# Revit family: HUNTER_I-40-06-SS
name_source: partatom
category: Sprinklers
revit_build: Autodesk Revit 2017 (Build: 20160225_1515(x64)
units: mm (PartAtom-declared; Revit-internal decimal feet)

## family parameters
Always vertical = Yes
Cut with Voids When Loaded = No
Maintain Annotation Orientation = No
OmniClass Number = 23.11.27.15.11.11
OmniClass Title = Installed Sprinkler Heads
Part Type = Normal
Room Calculation Point = No
Round Connector Dimension = Use Diameter
Shared = Yes
Work Plane-Based = No

## types (12) — shared parameters
Arc Max = 360.00°
Arc Min = 50.00°
Assembly Code = G2050700
Body Height = 200 mm  [stored 0.656168 ft]
Body Material = Hunter® ABS Plastic
Connection_Dia = 30 mm  [stored 0.0984252 ft]
Diameter = 610 mm
Exposed Diameter = 50 mm  [stored 0.164042 ft]
Inlet Size = 1" BSP
Keynote = 328423.02
Manufacturer = Hunter® Industries
Pop Up Height = 100 mm  [stored 0.328084 ft]
Pop Up Material = Hunter® Stainless Steel
Show 2D Symbol = Yes
Show Water Spray = Yes
Trajectory Angle = 25.00°
Type Comments = Rotor I-40-04 with Plastic Riser
Type Image = <None>
URL = https://www.hunterindustries.com
Water = Water
Water Pattern = Water Arc

## per-type parameters (varying)
| type | Description | Model | Nozzle Size | Nozzle Tag | Precipitation Rate | Pressure | Trajectory Radius |
| I-40-06-SS-Standard 10 Lt.Green-5.0bar-15.50m | Hunter I-40-04 Rotor Body with Preinstalled Check in Valve, stainless steel riser and (10 Lt. Green) Standard Nozzle | I-40-04-SS- Standard 10 Lt. Green | Hunter® (10 Lt. Green) Standard Nozzle | I-40-06-SS-10 Lt. Green | 21 mm/hr | 500.0 kPa | 16200 mm  [stored 53.1496 ft] |
| I-40-06-SS-Standard 13 Lt. Blue-5.0bar-15.80m | Hunter I-40-04 Rotor Body with Preinstalled Check in Valve, stainless steel riser and (13 Lt. Blue) Standard Nozzle | I-40-04-SS- Standard 13 Lt. Blue | Hunter® (13 Lt. Blue) Standard Nozzle | I-40-06-SS-113 Lt. Blue | 22 mm/hr | 500.0 kPa | 16800 mm |
| I-40-06-SS-Standard 15 Grey-5.0bar-17.40m | Hunter I-40-04 Rotor Body with Preinstalled Check in Valve, stainless steel riser and (15 Grey) Standard Nozzle | I-25-40-SS- Standard 15 Grey | Hunter® (15 Grey) Standard Nozzle | I-40-06-SS-15 Grey | 23 mm/hr | 500.0 kPa | 17400 mm |
| I-40-06-SS-Standard 8 Lt. Brown-5.0bar-14.30m | Hunter I-40-04 Rotor Body with Preinstalled Check in Valve, stainless steel riser and (8 Lt. Brown) Standard Nozzle | I-40-04-SS- Standard 8 Lt. Brown | Hunter® (08 Lt. Brown) Standard Nozzle | I-40-06-SS-18 Lt. Brown | 22 mm/hr | 500.0 kPa | 14300 mm  [stored 46.916 ft] |
| I-40-06-SS-Standard 23 Dk. Green-5.50bar-19.80m | Hunter I-40-04 Rotor Body with Preinstalled Check in Valve, stainless steel riser and (23 Dk. Green) Standard Nozzle | I-40-04-SS- Standard 23 Dk. Green | Hunter® (23 Dk. Green) Standard Nozzle | I-40-06-SS-23 Dk. Green | 29 mm/hr | 550.0 kPa | 19800 mm  [stored 64.9606 ft] |
| I-40-06-SS-Standard 25 Dk. Blue-6.0bar-21.00m | Hunter I-40-04 Rotor Body with Preinstalled Check in Valve, stainless steel riser and (25 Dk. Blue) Standard Nozzle | I-40-04-SS- Standard 25 Dk. Blue | Hunter® (25 Dk. Blue) Standard Nozzle | I-40-06-SS-25 Dk. Blue | 30 mm/hr | 600.0 kPa | 21000 mm  [stored 68.8976 ft] |
| I-40-06-SS-High speed 8 Lt.Brown-5.0bar-13.40m | Hunter I-40-04 Rotor Body with Preinstalled Check in Valve, stainless steel riser and (8 Lt. Brown) High Speedd Nozzle | I-40-04-SS-High Speed 8 Lt. Brown | Hunter® (8 Lt. Brown) High Speed Nozzle | I-40-06-SS-High Speed 8 Lt. Brown | 24 mm/hr | 500.0 kPa | 13400 mm  [stored 43.9633 ft] |
| I-40-06-SS-High speed 10 Lt.Green-5.0bar-14.30m | Hunter I-40-04 Rotor Body with Preinstalled Check in Valve, stainless steel riser and (10 Lt. Green) High Speed Nozzle | I-40-04-SS-High Speed 10 Lt. Green | Hunter® (10 Lt. Green) High Speed Nozzle | I-40-06-SS-High Speed 10 Lt. Green | 25 mm/hr | 500.0 kPa | 14300 mm  [stored 46.916 ft] |
| I-40-06-SS-High speed 13 Lt. Blue-5.0bar-14.60m | Hunter I-40-04 Rotor Body with Preinstalled Check in Valve, stainless steel riser and (13 Lt. Blue) High Speed Nozzle | I-40-04-SS-High Speed 13 Lt. Blue | Hunter® (13 Lt. Blue) High Speed Nozzle | I-40-06-SS-High Speed 13 Lt. Blue | 25 mm/hr | 500.0 kPa | 14600 mm  [stored 47.9003 ft] |
| I-40-06-SS-High speed 15 Grey-5.0bar-16.20m | Hunter I-40-04 Rotor Body with Preinstalled Check in Valve, stainless steel riser and (15 Grey) High Speed Nozzle | I-40-04-SS-High Speed 15 Grey | Hunter® (15 Grey) High Speed Nozzle | I-40-06-SS-High Speed 15 Grey | 27 mm/hr | 500.0 kPa | 16200 mm  [stored 53.1496 ft] |
| I-40-06-SS-High speed 23 Dk. Green-5.50bar-18.00m | Hunter I-40-04 Rotor Body with Preinstalled Check in Valve, stainless steel riser and (23 Dk. Green) High Speed Nozzle | I-40-04-SS-High Speed 23 Dk. Green | Hunter® (23 Dk. Green) High Speed Nozzle | I-40-06-SS-High Speed 23 Dk. Green | 35 mm/hr | 550.0 kPa | 18000 mm |
| I-40-06-SS-High speed 25 Dk. Blue-6.0bar-19.20m | Hunter I-40-04 Rotor Body with Preinstalled Check in Valve, stainless steel riser and (25 Dk. Blue) High Speed Nozzle | I-40-04-SS-High Speed 25 Dk. Blue | Hunter® (25 Dk. Blue) High Speed Nozzle | I-40-06-SS-High Speed 25 Dk. Blue | 34 mm/hr | 600.0 kPa | 19200 mm |

note: [stored X ft] marks values corroborated as IEEE doubles in the binary element streams (Revit-internal decimal feet)

## geometry (parser evidence)
native form markers: Sweep x11
no freeform markers — native parametric forms only
